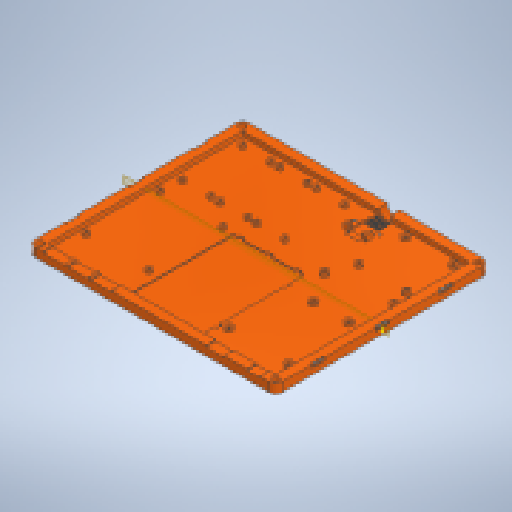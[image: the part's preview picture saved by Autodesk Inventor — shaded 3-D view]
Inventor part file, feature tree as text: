
AUTODESK INVENTOR PART (.ipt)
format: ipt  version: 2025.2 (Build 292293000, 293)  size: 842,240 bytes
history: native  units: mm
features: extrude x14, sketch x12, plane x4, mirror x3, fillet x2, pattern_linear x1, hole x1
ambient origin geometry x8: Origin, YZ Plane, XZ Plane, XY Plane, X Axis, Y Axis, Z Axis, Center Point
bodies: Solid1 (feature_tree)
feature tree (37):
  sketch  "Sketch1"  dims[d10=1.8mm d11=3.5mm]
  extrude  "Extrusion1"  Depth=3.5mm
  extrude  "Extrusion2"  Depth=4.0mm TaperAngle=0.0deg
  extrude  "Extrusion5"  Depth=5.0mm
  extrude  "Extrusion3"  Depth=7.5mm
  fillet  "Fillet1"  Radius=3.1mm
  extrude  "Extrusion4"  Depth=7.5mm
  plane  "Work Plane5"
  sketch  "Sketch3"  dims[d63=1.5mm d73=7.5mm]
  plane  "Work Plane2"
  extrude  "Extrusion6"  Depth=7.5mm
  pattern_linear  "Rectangular Pattern2"  Spacing1=45.72mm  [1 undecoded]
  plane  "Work Plane3"
  mirror  "Mirror2"
  sketch  "Sketch4"  dims[d83=15.24mm]
  extrude  "Extrusion7"  Depth=0.5mm
  hole  "Hole1"  [1 undecoded]
  sketch  "Sketch5"  dims[d84=90.17mm]
  mirror  "Mirror3"
  mirror  "Mirror4"
  sketch  "Sketch6"  dims[d85=96.52mm]
  extrude  "Extrusion8"  Depth=0.5mm
  extrude  "Extrusion9"  Depth=1.5mm
  extrude  "Extrusion10"  Depth=3.5mm
  extrude  "Extrusion11"  Depth=3.5mm
  extrude  "Extrusion13"  Depth=3.5mm
  extrude  "DC Jack Test Fit"  Depth=0.5mm
  fillet  "Fillet2"  Radius=7.5mm
  extrude  "Extrusion14"  Depth=65.0mm
  sketch  "Sketch2"  dims[d37=2.0mm d38=0.0mm d39=5.0mm]
  sketch  "Sketch Rectangular Pattern1"  dims[d19=3.0mm d20=0.0mm d21=4.0mm d22=0.0mm]
  sketch  "Sketch Rectangular Pattern2"  dims[d49=53.34mm d59=7.5mm d62=3.1mm]
  sketch  "Sketch Rectangular Pattern3"  dims[d79=7.5mm d82=2.54mm]
  plane  "Work Plane4"
  sketch  "Sketch7"  dims[d86=50.8mm]
  sketch  "Sketch8"  dims[d87=66.04mm]
  sketch  "Sketch9"  dims[d88=17.78mm d89=45.72mm d90=13.97mm d91=85.0mm d92=58.0mm d95=1.5mm d96=3.5mm d97=3.5mm d98=3.5mm d99=56.0mm d102=7.5mm d103=65.0mm d104=17.4mm d107=16.1mm d109=16.0mm d110=1.0mm d111=0.0mm d113=13.64mm d114=1.5mm d115=21.0mm d116=39.0mm d117=8.5mm d118=40.5mm d119=10.33mm d121=54.75mm d122=81.68mm d123=1.0mm d124=43.0mm d131=51.0mm d134=101.6mm d135=26.0mm d141=49.0mm d142=30.0mm d144=29.0mm d145=10.0mm d147=10.0mm d149=0.5mm d150=4.0mm d151=1.5mm d152=30.0mm d154=22.7mm d155=10.0mm d157=10.0mm d160=11.9mm d161=5.0mm d163=20.0mm d165=54.53mm d166=10.0mm d168=10.0mm d170=1.0mm d171=0.0mm d172=5.0mm d173=5.0mm d174=2.0mm d176=2.8mm d178=2.0mm d179=3.32mm d180=2.871mm d181=40.244mm d182=40.057mm d183=5.0mm d184=2.0mm d190=10.0mm d191=0.0mm d201=1.0mm d205=5.7mm d206=4.5mm d207=4.5mm d208=1.0mm d209=0.0mm d210=2.5mm d211=1.0mm d212=30.0mm d214=50.0mm d215=3.0mm d216=6.0mm d217=5.0mm d218=3.2mm d219=90.0deg d220=8.0mm d221=20.594885mm d222=45.0deg d223=10.5mm d224=14.0mm d226=1.6mm d227=0.8mm d228=1.2mm d229=0.8mm d230=1.2mm d231=0.8mm d232=1.2mm d235=0.8mm d239=75.0mm d240=6.0mm d241=0.8mm d242=1.2mm d243=6.0mm d244=0.0mm d245=0.5mm d246=0.0mm d247=1.0mm d248=0.0mm d249=5.0mm d250=10.0mm d251=0.0mm d252=0.0mm d253=10.5mm d254=4.5mm d255=1.2mm d256=25.0mm d257=35.0mm d258=9.95mm d259=0.0mm d260=0.8mm d261=13.0mm d262=9.5mm d263=4.5mm d265=2.0mm d266=2.0mm d267=3.0mm d268=1.5mm d269=1.0mm d270=0.0mm d271=0.75mm d272=20.0mm d273=2.0mm d274=8.0mm d275=10.0mm d276=0.0mm d278=1.5mm d279=2.0mm d280=2.0mm d281=1.8mm d282=4.8mm d74=0.5mm d75=0.872665mm d76=0.5mm d77=0.872665mm d225=0.872665mm]
note: 2 required parameter values undecoded (feature->parameter linkage not recoverable at this tier; creation-order binding heuristic only, values carry confidence <= 0.55)
